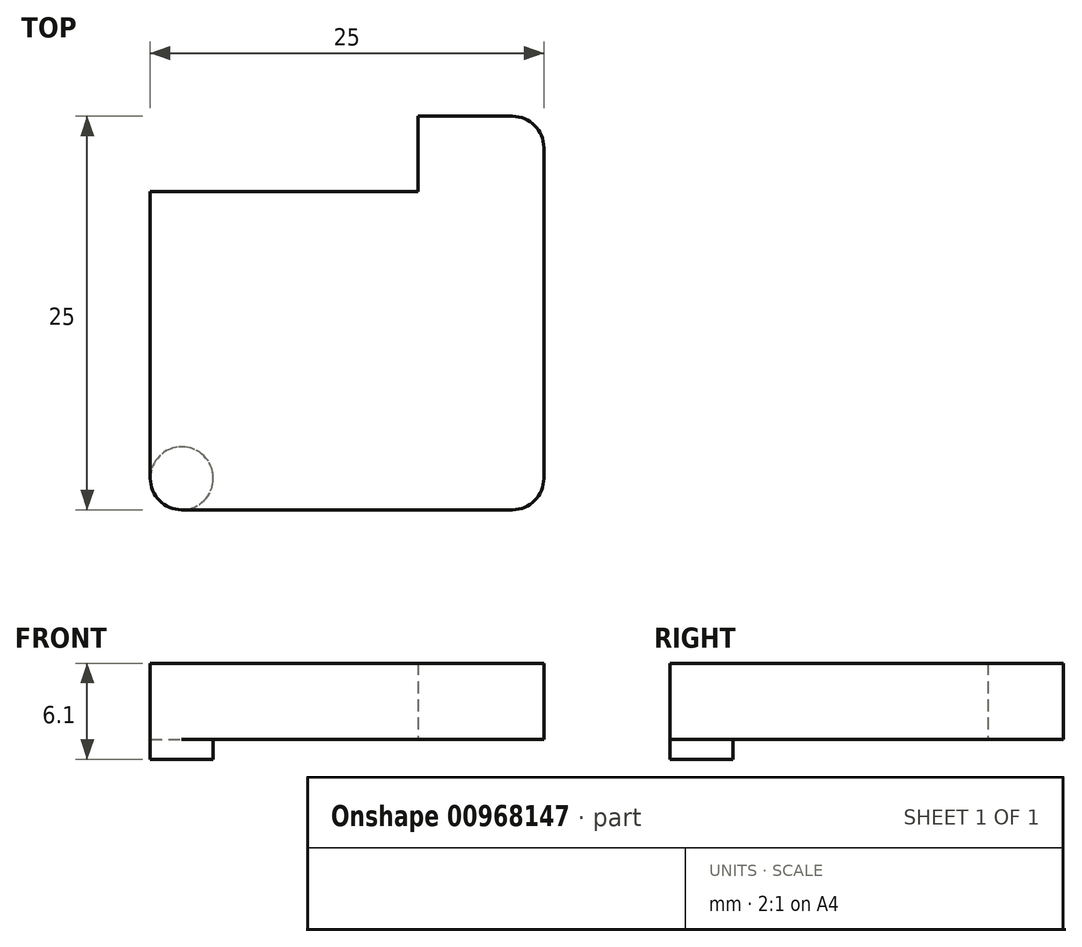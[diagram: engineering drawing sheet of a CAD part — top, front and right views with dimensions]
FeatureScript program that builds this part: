
annotation { "Feature Type Name" : "Feature", "Feature Type Description" : "" }
export const myFeature = defineFeature(function(context is Context, id is Id, definition is map)
    precondition{}
    {
        {
            var Q0;
            Q0=qCreatedBy(makeId("Top.planeOp"),FACE);
            var sketch = newSketch(context, id + "F0", { "sketchPlane" : qUnion([Q0])});
            skLineSegment(sketch, "E0.bottom", {"start": v(10.5, 12.5) * mm, "end": v(-10.5, 12.5) * mm});
            skLineSegment(sketch, "E0.top", {"start": v(10.5, -12.5) * mm, "end": v(-10.5, -12.5) * mm});
            skLineSegment(sketch, "E0.left", {"start": v(12.5, 10.5) * mm, "end": v(12.5, -10.5) * mm});
            skLineSegment(sketch, "E0.right", {"start": v(-12.5, 10.5) * mm, "end": v(-12.5, -10.5) * mm});
            skPoint(sketch, "E0.middle", {"position": v(0, 0) * mm});
            skLineSegment(sketch, "E1", {"start": v(-12.5, 7.7) * mm, "end": v(4.5, 7.7) * mm});
            skLineSegment(sketch, "E2", {"start": v(4.5, 7.7) * mm, "end": v(4.5, 12.5) * mm});
            skPoint(sketch, "E3.visualSharp", {"position": v(12.5, -12.5) * mm});
            skArc(sketch, "E3.filletArc", {"start": v(10.5, -12.5) * mm, "mid": v(11.91, -11.91) * mm, "end": v(12.5, -10.5) * mm});
            skPoint(sketch, "E4.visualSharp", {"position": v(-12.5, -12.5) * mm});
            skArc(sketch, "E4.filletArc", {"start": v(-12.5, -10.5) * mm, "mid": v(-11.91, -11.91) * mm, "end": v(-10.5, -12.5) * mm});
            skPoint(sketch, "E5.visualSharp", {"position": v(-12.5, 12.5) * mm});
            skArc(sketch, "E5.filletArc", {"start": v(-10.5, 12.5) * mm, "mid": v(-11.91, 11.91) * mm, "end": v(-12.5, 10.5) * mm});
            skPoint(sketch, "E6.visualSharp", {"position": v(12.5, 12.5) * mm});
            skArc(sketch, "E6.filletArc", {"start": v(12.5, 10.5) * mm, "mid": v(11.91, 11.91) * mm, "end": v(10.5, 12.5) * mm});
            skSolve(sketch);
        }
        {
            var Q0;
            Q0=makeQuery(id+"F0.imprint","IMPRINT",FACE,{"disambiguationData":[TD([[makeQuery(id+"F0.imprint","IMPRINT",EDGE,{"derivedFrom":sQuery(id+"F0.wireOp",EDGE,"E0.top")}),-1.0]])]});
            var Q1;
            Q1=makeQuery(id+"F0.imprint","IMPRINT",FACE,{"disambiguationData":[TD([[makeQuery(id+"F0.imprint","IMPRINT",EDGE,{"derivedFrom":sQuery(id+"F0.wireOp",EDGE,"Fkv3pkIO-kSXM-xOpH-B9we-DmDPvZ3BCUb3")}),1.0]])]});
            var Q2;
            Q2=makeQuery(id+"F0.imprint","IMPRINT",FACE,{"disambiguationData":[TD([[makeQuery(id+"F0.imprint","IMPRINT",EDGE,{"derivedFrom":sQuery(id+"F0.wireOp",EDGE,"o93UMpO4-4z2h-cB08-UtpR-NBYZhi7vGJAb")}),1.0]])]});
            extrude(context, id + "F1", {"entities" : qUnion([Q0, Q1, Q2]), "depth" : 6.1 * mm, "offsetDistance" : 25 * mm});
        }
        {
            var Q0;
            Q0=makeQuery(id+"F1.opExtrude","CAP_FACE",FACE,{"disambiguationData":[OSD([sQuery(id+"F0.wireOp",EDGE,"E0.bottom"),sQuery(id+"F0.wireOp",EDGE,"E0.top"),sQuery(id+"F0.wireOp",EDGE,"E0.left"),sQuery(id+"F0.wireOp",EDGE,"E0.right"),sQuery(id+"F0.wireOp",EDGE,"E1"),sQuery(id+"F0.wireOp",EDGE,"E2"),sQuery(id+"F0.wireOp",EDGE,"E3.filletArc"),sQuery(id+"F0.wireOp",EDGE,"E4.filletArc"),sQuery(id+"F0.wireOp",EDGE,"E6.filletArc")])],"isStart":true});
            var sketch = newSketch(context, id + "F2", { "sketchPlane" : qUnion([Q0])});
            skCircle(sketch, "E7", {"center": v(10.5, -10.5) * mm, "radius": 2 * mm});
            skCircle(sketch, "E8", {"center": v(-10.5, 10.5) * mm, "radius": 2 * mm});
            skSolve(sketch);
        }
        {
            var Q0;
            {var subQ0=sQuery(id+"F2.wireOp",EDGE,"E7");Q0=makeQuery(id+"F2.imprint","IMPRINT",FACE,{"disambiguationData":[TD([[makeQuery(id+"F2.imprint","IMPRINT",EDGE,{"disambiguationData":[OD(0.0)],"derivedFrom":subQ0}),-1.0]])]});}
            var Q1;
            {var subQ0=sQuery(id+"F2.wireOp",EDGE,"E8");Q1=makeQuery(id+"F2.imprint","IMPRINT",FACE,{"disambiguationData":[TD([[makeQuery(id+"F2.imprint","IMPRINT",EDGE,{"disambiguationData":[OD(0.0)],"derivedFrom":subQ0}),-1.0]])]});}
            extrude(context, id + "F3", {"entities" : qUnion([Q0, Q1]), "operationType" : NewBodyOperationType.REMOVE, "oppositeDirection" : true, "depth" : 1.25 * mm, "offsetDistance" : 25 * mm});
        }
    });
